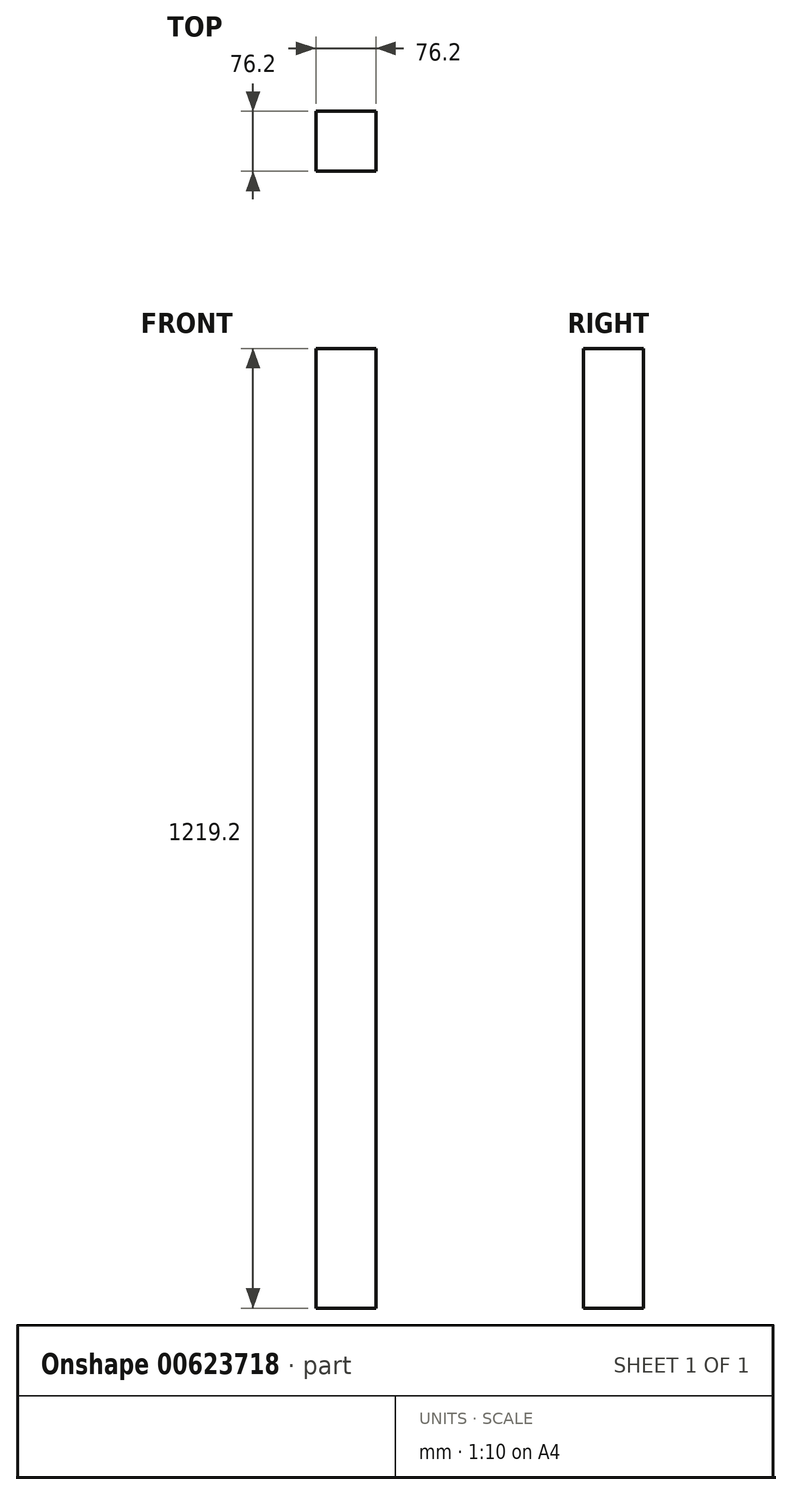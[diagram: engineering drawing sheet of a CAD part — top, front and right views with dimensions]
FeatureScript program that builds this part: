
annotation { "Feature Type Name" : "Feature", "Feature Type Description" : "" }
export const myFeature = defineFeature(function(context is Context, id is Id, definition is map)
    precondition{}
    {
        {
            var Q0;
            Q0=qCreatedBy(makeId("Front.planeOp"),FACE);
            var sketch = newSketch(context, id + "F0", { "sketchPlane" : qUnion([Q0])});
            skLineSegment(sketch, "E0.bottom", {"start": v(38.1, 609.6) * mm, "end": v(-38.1, 609.6) * mm});
            skLineSegment(sketch, "E0.top", {"start": v(38.1, -609.6) * mm, "end": v(-38.1, -609.6) * mm});
            skLineSegment(sketch, "E0.left", {"start": v(38.1, 609.6) * mm, "end": v(38.1, -609.6) * mm});
            skLineSegment(sketch, "E0.right", {"start": v(-38.1, 609.6) * mm, "end": v(-38.1, -609.6) * mm});
            skPoint(sketch, "E0.middle", {"position": v(0, 0) * mm});
            skSolve(sketch);
        }
        {
            var Q0;
            Q0 = qSketchRegion(id + "F0", true);
            extrude(context, id + "F1", {"entities" : qUnion([Q0]), "depth" : 76.2 * mm, "offsetDistance" : 25.4 * mm});
        }
    });
